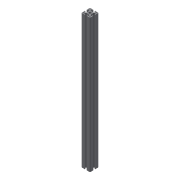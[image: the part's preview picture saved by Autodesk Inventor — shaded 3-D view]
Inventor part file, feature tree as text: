
AUTODESK INVENTOR PART (.ipt)
format: ipt  version: 2016 (Build 200138000, 138)  size: 184,320 bytes
history: native  units: mm
features: other x42, sketch x5, hole x4, extrude x1
ambient origin geometry x8: Origin, YZ Plane, XZ Plane, XY Plane, X Axis, Y Axis, Z Axis, Center Point
bodies: Solid1 (feature_tree)
feature tree (52):
  extrude  "Extrusion1"  [1 undecoded]
  hole  "Drilling 1"  [1 undecoded]
  hole  "Drilling 2"  [1 undecoded]
  hole  "Drilling 3"  [1 undecoded]
  hole  "Drilling 4"  [1 undecoded]
  other  "side_4d_XY"
  other  "side_4d_YZ"
  other  "side_4d_ZX"
  other  "side_4d_X"
  other  "side_4d_Y"
  other  "side_4d_Z"
  other  "side_4d_Center"
  other  "side_1a_XY"
  other  "side_1a_YZ"
  other  "side_1a_ZX"
  other  "side_1a_X"
  other  "side_1a_Y"
  other  "side_1a_Z"
  other  "side_1a_Center"
  other  "side_2b_XY"
  other  "side_2b_YZ"
  other  "side_2b_ZX"
  other  "side_2b_X"
  other  "side_2b_Y"
  other  "side_2b_Z"
  other  "side_2b_Center"
  other  "side_3c_XY"
  other  "side_3c_YZ"
  other  "side_3c_ZX"
  other  "side_3c_X"
  other  "side_3c_Y"
  other  "side_3c_Z"
  other  "side_3c_Center"
  other  "end_XY"
  other  "end_YZ"
  other  "end_ZX"
  other  "end_X"
  other  "end_Y"
  other  "end_Z"
  other  "end_Center"
  other  "start_XY"
  other  "start_YZ"
  other  "start_ZX"
  other  "start_X"
  other  "start_Y"
  other  "start_Z"
  other  "start_Center"
  sketch  "Skizze_1"  dims[d0=620.0mm d1=0.0mm]
  sketch  "Sketch2"  dims[d2=5.0mm d3=6.0mm d4=4.0mm d5=2.0mm d6=90.0deg d7=6000.0mm d8=0.0mm]
  sketch  "Sketch3"  dims[d9=5.0mm d10=6.0mm d11=4.0mm d12=2.0mm d13=90.0deg d14=6000.0mm d15=0.0mm]
  sketch  "Sketch4"  dims[d16=5.0mm d17=6.0mm d18=4.0mm d19=2.0mm d20=90.0deg d21=6000.0mm d22=0.0mm]
  sketch  "Sketch5"  dims[d23=5.0mm d24=6.0mm d25=4.0mm d26=2.0mm d27=90.0deg d28=6000.0mm d29=0.0mm]
note: 5 required parameter values undecoded (feature->parameter linkage not recoverable at this tier; creation-order binding heuristic only, values carry confidence <= 0.55)
